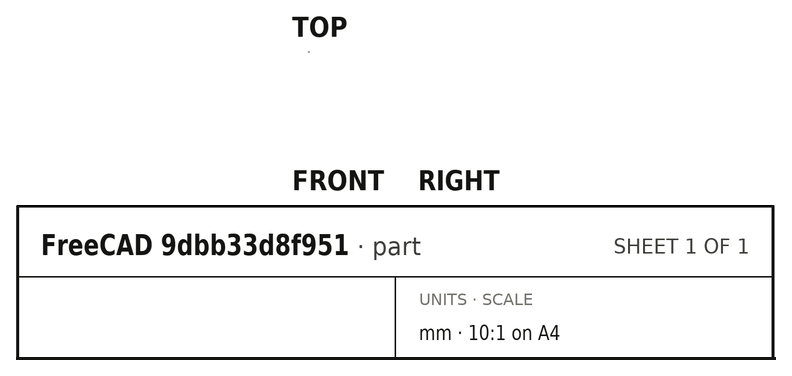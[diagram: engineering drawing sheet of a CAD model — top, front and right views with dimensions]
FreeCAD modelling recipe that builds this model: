
FCSTD DOCUMENT  (FreeCAD 0.21R33694 (Git))
Label: coax
License: All rights reserved
LicenseURL: http://en.wikipedia.org/wiki/All_rights_reserved
objects: Part::Part2DObjectPython×5, App::FeaturePython×3, Part::Cut×1, Part::MultiCommon×1
note: 7 computed .brp shape members not serialized (recipe doc carries the construction recipe); baked Part::Feature solids carry a one-line shape summary decoded from their .brp

FEATURE [Part::Part2DObjectPython] Circle  # Draft 2D object (typed FeaturePython)
  Area = 6.88134e-06
  FirstAngle = 0
  LastAngle = 0
  MakeFace = true
  Radius = 0.00148
FEATURE [Part::Part2DObjectPython] Circle001  # Draft 2D object (typed FeaturePython)
  Area = 5.17848e-07
  FirstAngle = 0
  LastAngle = 0
  MakeFace = true
  Radius = 0.000406
FEATURE [Part::Cut] Cut
  Base = -> Circle
  Tool = -> Circle001
FEATURE [Part::Part2DObjectPython] Line  label="_P1"  # Draft 2D object (typed FeaturePython)
  Area = 0
  ChamferSize = 0
  Closed = false
  End = (0.00148,0,0)
  FilletRadius = 0
  Length = 0.001074
  MakeFace = true
  Placement = pos=(0.000406,0,0) rot=(0,0,1;0rad)
  Points = (2) [(0,0,0),(0.001074,0,0)]
  Start = (0.000406,0,0)
  Subdivisions = 0
FEATURE [App::FeaturePython] Text  label="_M1(voltage){2}"  # WARN: FeaturePython — macro-defined, semantics opaque (R4)
  Placement = pos=(0.000624029,-0.00216561,0) rot=(0,0,1;0rad)
  Text = .
FEATURE [Part::Part2DObjectPython] Wire  # Draft 2D object (typed FeaturePython)
  Area = 5e-05
  ChamferSize = 0
  Closed = true
  End = (0,0,0)
  FilletRadius = 0
  Length = 0.0341421
  MakeFace = true
  Points = (4) [(0,0,0),(0.01,3.06162e-19,0),(0.01,0.01,0),(0,0,0)]
  Start = (0,0,0)
  Subdivisions = 0
FEATURE [Part::MultiCommon] Common  label="slice"
  Shapes = -> [Cut,Wire]
FEATURE [Part::Part2DObjectPython] Line001  label="_P2"  # Draft 2D object (typed FeaturePython)
  Area = 0
  ChamferSize = 0
  Closed = false
  End = (0.00104652,0.00104652,0)
  FilletRadius = 0
  Length = 0.001074
  MakeFace = true
  Placement = pos=(0.000287085,0.000287085,0) rot=(0,0,1;0rad)
  Points = (2) [(0,0,0),(0.000759433,0.000759433,0)]
  Start = (0.000287085,0.000287085,0)
  Subdivisions = 0
FEATURE [App::FeaturePython] Text001  label="_B1(PMC){1}"  # WARN: FeaturePython — macro-defined, semantics opaque (R4)
  Placement = pos=(0.00119715,-0.000671772,0) rot=(0,0,1;0rad)
  Text = .
FEATURE [App::FeaturePython] Text002  label="_B2(PMC){2}"  # WARN: FeaturePython — macro-defined, semantics opaque (R4)
  Placement = pos=(0.00124922,-0.000408862,0) rot=(0,0,1;0rad)
  Text = .
